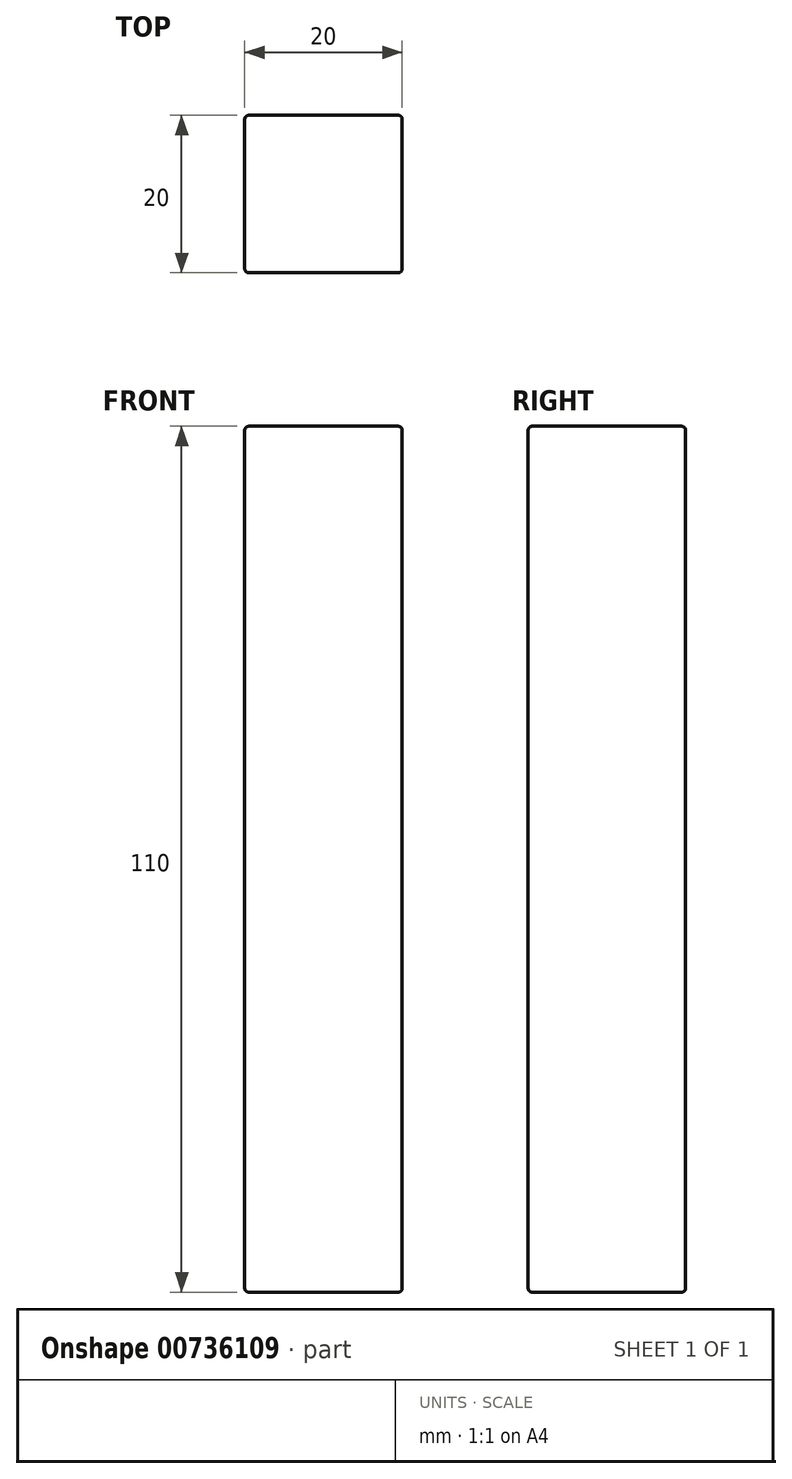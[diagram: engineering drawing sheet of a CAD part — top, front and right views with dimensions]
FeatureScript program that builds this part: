
annotation { "Feature Type Name" : "Feature", "Feature Type Description" : "" }
export const myFeature = defineFeature(function(context is Context, id is Id, definition is map)
    precondition{}
    {
        {
            var Q0;
            Q0=qCreatedBy(makeId("Front.planeOp"),FACE);
            var sketch = newSketch(context, id + "F0", { "sketchPlane" : qUnion([Q0])});
            skLineSegment(sketch, "E0.bottom", {"start": v(-10, 55) * mm, "end": v(10, 55) * mm});
            skLineSegment(sketch, "E0.top", {"start": v(-10, -55) * mm, "end": v(10, -55) * mm});
            skLineSegment(sketch, "E0.left", {"start": v(-10, 55) * mm, "end": v(-10, -55) * mm});
            skLineSegment(sketch, "E0.right", {"start": v(10, 55) * mm, "end": v(10, -55) * mm});
            skPoint(sketch, "E0.middle", {"position": v(0, 0) * mm});
            skSolve(sketch);
        }
        {
            var Q0;
            Q0 = qSketchRegion(id + "F0", true);
            extrude(context, id + "F1", {"entities" : qUnion([Q0]), "depth" : 20 * mm, "offsetDistance" : 25 * mm});
        }
        {
            var Q0;
            Q0=makeQuery(id+"F1.opExtrude","CAP_FACE",FACE,{"disambiguationData":[OSD([sQuery(id+"F0.wireOp",EDGE,"E0.bottom"),sQuery(id+"F0.wireOp",EDGE,"E0.top"),sQuery(id+"F0.wireOp",EDGE,"E0.left"),sQuery(id+"F0.wireOp",EDGE,"E0.right")])],"isStart":false});
            var Q1;
            Q1=makeQuery(id+"F1.opExtrude","SWEPT_FACE",FACE,{"disambiguationData":[OSD([sQuery(id+"F0.wireOp",EDGE,"E0.top")])]});
            var Q2;
            Q2=makeQuery(id+"F1.opExtrude","CAP_FACE",FACE,{"disambiguationData":[OSD([sQuery(id+"F0.wireOp",EDGE,"E0.bottom"),sQuery(id+"F0.wireOp",EDGE,"E0.top"),sQuery(id+"F0.wireOp",EDGE,"E0.left"),sQuery(id+"F0.wireOp",EDGE,"E0.right")])],"isStart":true});
            var Q3;
            Q3=makeQuery(id+"F1.opExtrude","SWEPT_FACE",FACE,{"disambiguationData":[OSD([sQuery(id+"F0.wireOp",EDGE,"E0.bottom")])]});
            fillet(context, id + "F2", {"entities" : qUnion([Q0, Q1, Q2, Q3]), "radius" : 0.5 * mm, "tangentPropagation" : true, "allowEdgeOverflow" : false});
        }
    });
